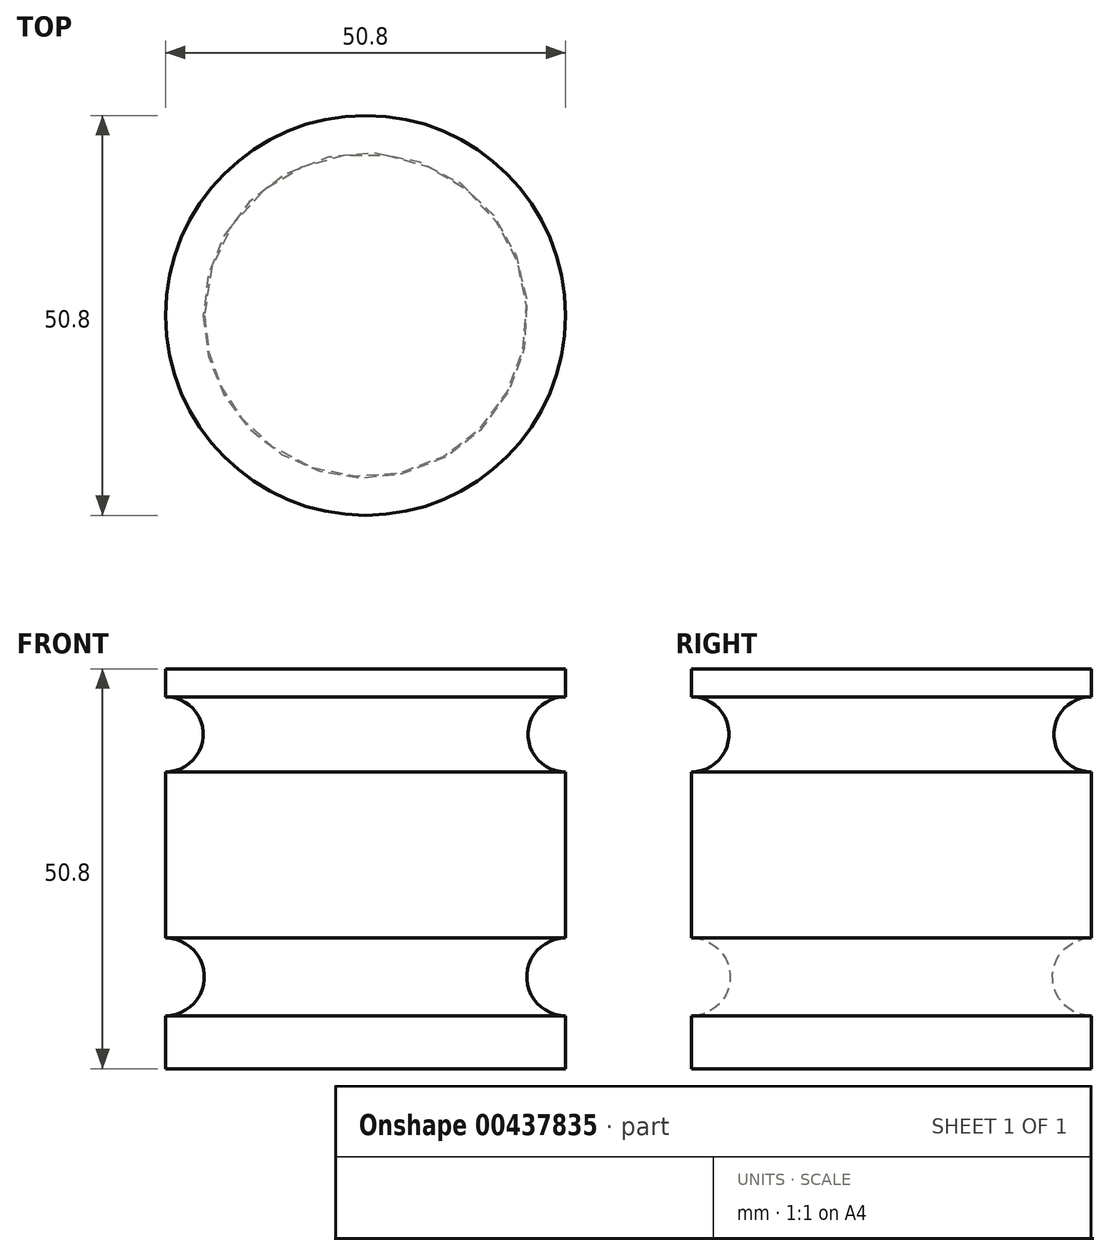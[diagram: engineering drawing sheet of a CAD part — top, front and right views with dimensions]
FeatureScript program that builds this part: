
annotation { "Feature Type Name" : "Feature", "Feature Type Description" : "" }
export const myFeature = defineFeature(function(context is Context, id is Id, definition is map)
    precondition{}
    {
        {
            var Q0;
            Q0=qCreatedBy(makeId("Front.planeOp"),FACE);
            var sketch = newSketch(context, id + "F0", { "sketchPlane" : qUnion([Q0])});
            skLineSegment(sketch, "E0.bottom", {"start": v(0, 0) * mm, "end": v(-25.4, 0) * mm});
            skLineSegment(sketch, "E0.top", {"start": v(0, 50.8) * mm, "end": v(-25.4, 50.8) * mm});
            skLineSegment(sketch, "E0.left", {"start": v(0, 0) * mm, "end": v(0, 6.72) * mm});
            skLineSegment(sketch, "E0.right", {"start": v(-25.4, 0) * mm, "end": v(-25.4, 50.8) * mm});
            skArc(sketch, "E1", {"start": v(0, 47.24) * mm, "mid": v(-4.77, 42.47) * mm, "end": v(0, 37.7) * mm});
            skArc(sketch, "E2", {"start": v(0, 16.59) * mm, "mid": v(-4.93, 11.66) * mm, "end": v(0, 6.72) * mm});
            skLineSegment(sketch, "E3.trimOffspring", {"start": v(0, 47.24) * mm, "end": v(0, 50.8) * mm});
            skLineSegment(sketch, "E4.trimOffspring", {"start": v(0, 16.59) * mm, "end": v(0, 37.7) * mm});
            skSolve(sketch);
        }
        {
            var Q0;
            Q0 = qSketchRegion(id + "F0", true);
            var Q1;
            Q1=sQuery(id+"F0.wireOp",EDGE,"E0.right");
            revolve(context, id + "F1", {"entities" : qUnion([Q0]), "axis" : qUnion([Q1]), "revolveType" : RevolveType.FULL});
        }
    });
